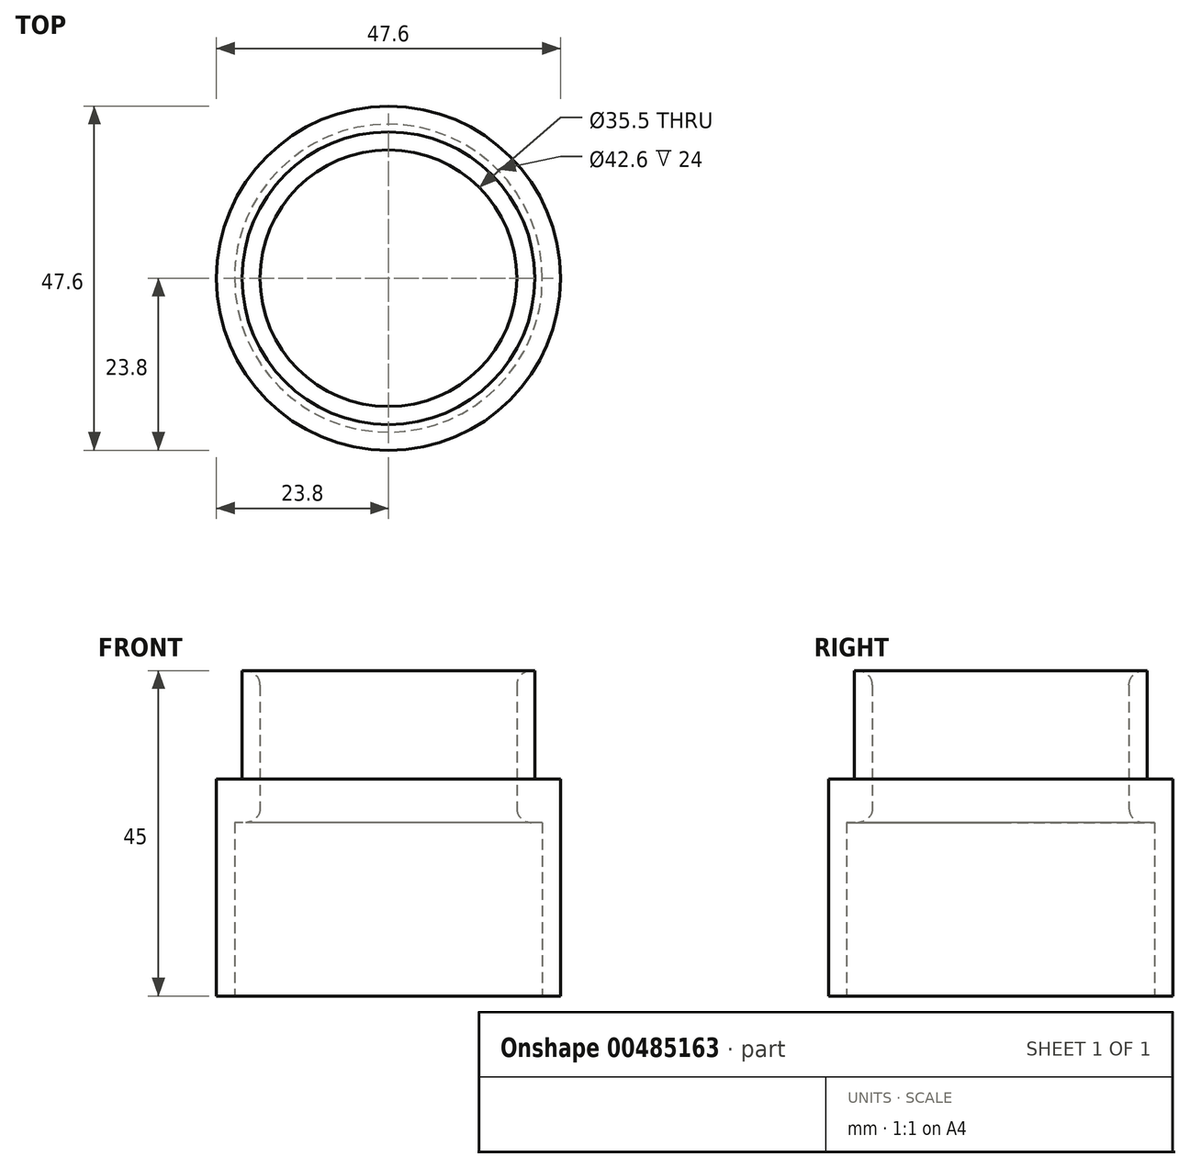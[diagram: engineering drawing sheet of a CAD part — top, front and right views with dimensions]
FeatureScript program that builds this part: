
annotation { "Feature Type Name" : "Feature", "Feature Type Description" : "" }
export const myFeature = defineFeature(function(context is Context, id is Id, definition is map)
    precondition{}
    {
        {
            var Q0;
            Q0=qCreatedBy(makeId("Top.planeOp"),FACE);
            var sketch = newSketch(context, id + "F0", { "sketchPlane" : qUnion([Q0])});
            skCircle(sketch, "E0", {"center": v(0, 0) * mm, "radius": 23.8 * mm});
            skCircle(sketch, "E1", {"center": v(0, 0) * mm, "radius": 20.25 * mm});
            skCircle(sketch, "E2", {"center": v(0, 0) * mm, "radius": 17.75 * mm});
            skSolve(sketch);
        }
        {
            var Q0;
            Q0=makeQuery(id+"F0.imprint","IMPRINT",FACE,{"disambiguationData":[TD([[makeQuery(id+"F0.imprint","IMPRINT",EDGE,{"derivedFrom":sQuery(id+"F0.wireOp",EDGE,"E1")}),1.0]])]});
            extrude(context, id + "F1", {"entities" : qUnion([Q0]), "depth" : 45 * mm, "offsetDistance" : 25 * mm});
        }
        {
            var Q0;
            Q0=makeQuery(id+"F0.imprint","IMPRINT",FACE,{"disambiguationData":[TD([[makeQuery(id+"F0.imprint","IMPRINT",EDGE,{"derivedFrom":sQuery(id+"F0.wireOp",EDGE,"E0")}),1.0]])]});
            extrude(context, id + "F2", {"entities" : qUnion([Q0]), "operationType" : NewBodyOperationType.ADD, "depth" : 30 * mm, "offsetDistance" : 25 * mm});
        }
        {
            var Q0;
            Q0=qCreatedBy(makeId("Top.planeOp"),FACE);
            var sketch = newSketch(context, id + "F3", { "sketchPlane" : qUnion([Q0])});
            skCircle(sketch, "E3", {"center": v(0, 0) * mm, "radius": 21.3 * mm});
            skSolve(sketch);
        }
        {
            var Q0;
            Q0 = qSketchRegion(id + "F3", true);
            extrude(context, id + "F4", {"entities" : qUnion([Q0]), "operationType" : NewBodyOperationType.REMOVE, "depth" : 24 * mm, "offsetDistance" : 25 * mm});
        }
        {
            var Q0;
            Q0=makeQuery(id+"F4.boolean.opBoolean","INTERSECT",EDGE,{"derivedFrom":[makeQuery(id+"F1.opExtrude","SWEPT_FACE",FACE,{"disambiguationData":[OSD([sQuery(id+"F0.wireOp",EDGE,"E2")])]}),makeQuery(id+"F4.opExtrude","CAP_FACE",FACE,{"disambiguationData":[OSD([sQuery(id+"F3.wireOp",EDGE,"E3")])],"isStart":false})]});
            var Q1;
            Q1=makeQuery(id+"F4.boolean.opBoolean","COPY",EDGE,{"derivedFrom":makeQuery(id+"F4.opExtrude","CAP_EDGE",EDGE,{"disambiguationData":[OSD([sQuery(id+"F3.wireOp",EDGE,"E3")])],"isStart":true})});
            var Q2;
            Q2=makeQuery(id+"F1.opExtrude","CAP_EDGE",EDGE,{"disambiguationData":[OSD([sQuery(id+"F0.wireOp",EDGE,"E2")])],"isStart":false});
            fillet(context, id + "F5", {"entities" : qUnion([Q0, Q1, Q2]), "radius" : 2 * mm, "tangentPropagation" : true, "allowEdgeOverflow" : false});
        }
    });
